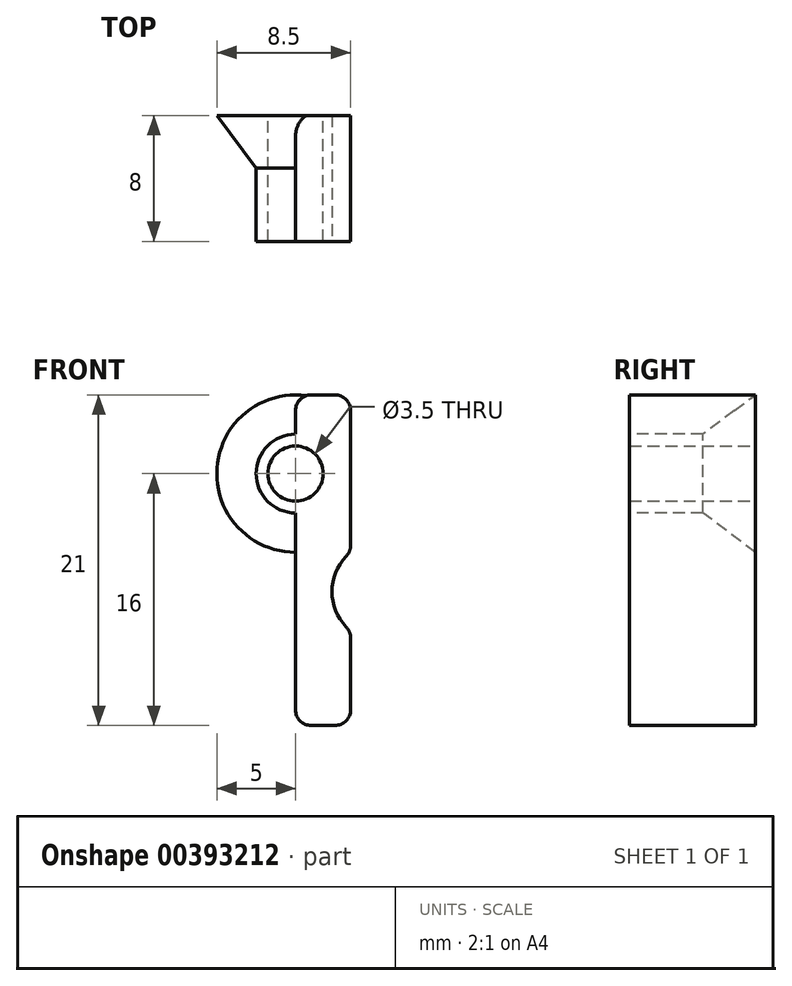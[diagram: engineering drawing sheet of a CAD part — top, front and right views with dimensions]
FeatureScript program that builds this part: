
annotation { "Feature Type Name" : "Feature", "Feature Type Description" : "" }
export const myFeature = defineFeature(function(context is Context, id is Id, definition is map)
    precondition{}
    {
        {
            var Q0;
            Q0=qCreatedBy(makeId("Top.planeOp"),FACE);
            var sketch = newSketch(context, id + "F0", { "sketchPlane" : qUnion([Q0])});
            skLineSegment(sketch, "E0.0", {"start": v(0, 8) * mm, "end": v(-5, 8) * mm});
            skLineSegment(sketch, "E1.0", {"start": v(-5, 8) * mm, "end": v(-1, 2.67) * mm});
            skLineSegment(sketch, "E2.0", {"start": v(-1, 0) * mm, "end": v(-1, 2.67) * mm});
            skLineSegment(sketch, "E3.0", {"start": v(0, 0) * mm, "end": v(-1, 0) * mm});
            skLineSegment(sketch, "E4.0", {"start": v(0, 0) * mm, "end": v(0, 8) * mm});
            skSolve(sketch);
        }
        {
            var Q0;
            Q0=makeQuery(id+"F0.imprint","IMPRINT",FACE,{"disambiguationData":[TD([[makeQuery(id+"F0.imprint","IMPRINT",EDGE,{"derivedFrom":sQuery(id+"F0.wireOp",EDGE,"E0.0")}),1.0]])]});
            var Q1;
            Q1=sQuery(id+"F0.wireOp",EDGE,"E4.0");
            revolve(context, id + "F1", {"entities" : qUnion([Q0]), "axis" : qUnion([Q1]), "revolveType" : RevolveType.SYMMETRIC, "angle" : 180 * degree});
        }
        {
            var Q0;
            Q0=qCreatedBy(makeId("Right.planeOp"),FACE);
            var sketch = newSketch(context, id + "F2", { "sketchPlane" : qUnion([Q0])});
            skLineSegment(sketch, "E5.bottom", {"start": v(0, 5.03) * mm, "end": v(8.05, 5.03) * mm});
            skLineSegment(sketch, "E5.top", {"start": v(0, -11.15) * mm, "end": v(8.05, -11.15) * mm});
            skLineSegment(sketch, "E5.left", {"start": v(0, 9.32) * mm, "end": v(0, -11.15) * mm});
            skLineSegment(sketch, "E5.right", {"start": v(8.05, 9.32) * mm, "end": v(8.05, -11.15) * mm});
            skSolve(sketch);
        }
        {
            var Q0;
            Q0=qCreatedBy(makeId("Front.planeOp"),FACE);
            var sketch = newSketch(context, id + "F3", { "sketchPlane" : qUnion([Q0])});
            skLineSegment(sketch, "E6", {"start": v(0, 5) * mm, "end": v(3.5, 5) * mm});
            skLineSegment(sketch, "E7", {"start": v(3.5, 5) * mm, "end": v(3.5, -5) * mm});
            skLineSegment(sketch, "E8", {"start": v(3.5, -5) * mm, "end": v(2.02, -5) * mm});
            skLineSegment(sketch, "E9.0", {"start": v(3.5, -10) * mm, "end": v(2.02, -10) * mm});
            skArc(sketch, "E10", {"start": v(3.5, -5) * mm, "mid": v(2.31, -7.5) * mm, "end": v(3.5, -10) * mm});
            skLineSegment(sketch, "E11", {"start": v(3.5, -10) * mm, "end": v(3.5, -16) * mm});
            skLineSegment(sketch, "E12", {"start": v(3.5, -16) * mm, "end": v(0, -16) * mm});
            skLineSegment(sketch, "E13", {"start": v(0, -16) * mm, "end": v(0, -2.5) * mm});
            skArc(sketch, "E14", {"start": v(0, 2.5) * mm, "mid": v(-2.5, 0) * mm, "end": v(0, -2.5) * mm});
            skLineSegment(sketch, "E15.trimOffspring", {"start": v(0, 2.5) * mm, "end": v(0, 5) * mm});
            skSolve(sketch);
        }
        {
            var Q0;
            Q0=makeQuery(id+"F3.imprint","IMPRINT",FACE,{"disambiguationData":[TD([[makeQuery(id+"F3.imprint","IMPRINT",EDGE,{"derivedFrom":sQuery(id+"F3.wireOp",EDGE,"E6")}),-1.0]])]});
            extrude(context, id + "F4", {"entities" : qUnion([Q0]), "operationType" : NewBodyOperationType.ADD, "oppositeDirection" : true, "depth" : 8 * mm});
        }
        {
            var Q0;
            Q0=makeQuery(id+"F4.boolean.opBoolean","MERGE",FACE,{"derivedFrom":[makeQuery(id+"F1.opRevolve","SWEPT_FACE",FACE,{"disambiguationData":[OSD([sQuery(id+"F0.wireOp",EDGE,"E0.0")])]}),makeQuery(id+"F4.opExtrude","CAP_FACE",FACE,{"disambiguationData":[OSD([sQuery(id+"F3.wireOp",EDGE,"E6"),sQuery(id+"F3.wireOp",EDGE,"E7"),sQuery(id+"F3.wireOp",EDGE,"E10"),sQuery(id+"F3.wireOp",EDGE,"E11"),sQuery(id+"F3.wireOp",EDGE,"E12"),sQuery(id+"F3.wireOp",EDGE,"E13")])],"isStart":false})]});
            var sketch = newSketch(context, id + "F5", { "sketchPlane" : qUnion([Q0])});
            skCircle(sketch, "E16", {"center": v(0, 0) * mm, "radius": 1.75 * mm});
            skSolve(sketch);
        }
        {
            var Q0;
            Q0=makeQuery(id+"F5.imprint","IMPRINT",FACE,{"disambiguationData":[TD([[makeQuery(id+"F5.imprint","IMPRINT",EDGE,{"derivedFrom":sQuery(id+"F5.wireOp",EDGE,"E16")}),1.0]])]});
            extrude(context, id + "F6", {"entities" : qUnion([Q0]), "operationType" : NewBodyOperationType.REMOVE, "oppositeDirection" : true, "depth" : 25 * mm});
        }
        {
            var Q0;
            Q0=makeQuery(id+"F4.opExtrude","SWEPT_EDGE",EDGE,{"disambiguationData":[OSD([sQuery(id+"F3.wireOp",EDGE,"E6"),sQuery(id+"F3.wireOp",EDGE,"E7")])]});
            var Q1;
            Q1=makeQuery(id+"F4.opExtrude","SWEPT_EDGE",EDGE,{"disambiguationData":[OSD([sQuery(id+"F3.wireOp",EDGE,"E12"),sQuery(id+"F3.wireOp",EDGE,"E13")])]});
            var Q2;
            Q2=makeQuery(id+"F4.opExtrude","SWEPT_EDGE",EDGE,{"disambiguationData":[OSD([sQuery(id+"F3.wireOp",EDGE,"E11"),sQuery(id+"F3.wireOp",EDGE,"E12")])]});
            var Q3;
            Q3=makeQuery(id+"F4.opExtrude","SWEPT_EDGE",EDGE,{"disambiguationData":[OSD([sQuery(id+"F3.wireOp",EDGE,"E10"),sQuery(id+"F3.wireOp",EDGE,"E11")])]});
            var Q4;
            Q4=makeQuery(id+"F4.opExtrude","SWEPT_EDGE",EDGE,{"disambiguationData":[OSD([sQuery(id+"F3.wireOp",EDGE,"E7"),sQuery(id+"F3.wireOp",EDGE,"E10")])]});
            fillet(context, id + "F7", {"entities" : qUnion([Q0, Q1, Q2, Q3, Q4]), "radius" : 1 * mm, "tangentPropagation" : true, "allowEdgeOverflow" : false});
        }
        {
            var Q0;
            Q0=makeQuery(id+"F4.opExtrude","SWEPT_EDGE",EDGE,{"disambiguationData":[OSD([sQuery(id+"F3.wireOp",EDGE,"E6"),sQuery(id+"F3.wireOp",EDGE,"E15.trimOffspring")])]});
            fillet(context, id + "F8", {"entities" : qUnion([Q0]), "radius" : 1 * mm, "tangentPropagation" : true, "allowEdgeOverflow" : false});
        }
    });
